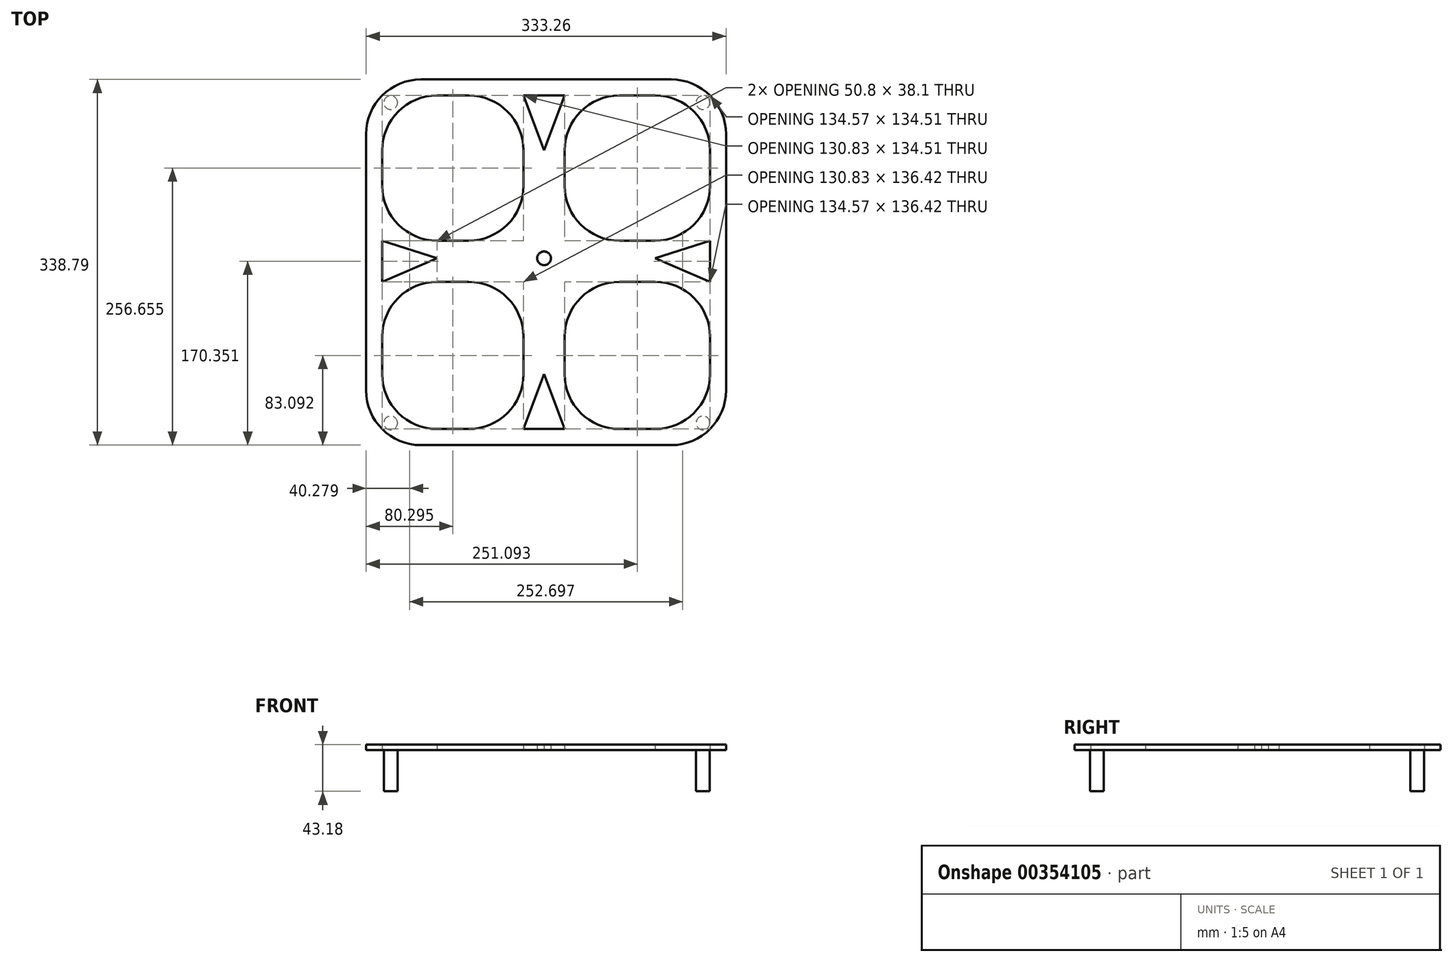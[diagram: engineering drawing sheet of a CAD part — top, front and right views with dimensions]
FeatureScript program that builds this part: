
annotation { "Feature Type Name" : "Feature", "Feature Type Description" : "" }
export const myFeature = defineFeature(function(context is Context, id is Id, definition is map)
    precondition{}
    {
        {
            var Q0;
            Q0=qCreatedBy(makeId("Top.planeOp"),FACE);
            var sketch = newSketch(context, id + "F0", { "sketchPlane" : qUnion([Q0])});
            skLineSegment(sketch, "E0.bottom", {"start": v(102.82, 16.36) * mm, "end": v(69.85, 16.36) * mm});
            skLineSegment(sketch, "E0.top", {"start": v(102.82, -21.74) * mm, "end": v(69.85, -21.74) * mm});
            skPoint(sketch, "E0.middle", {"position": v(0, 0) * mm});
            skLineSegment(sketch, "E1.left", {"start": v(19.05, 100.07) * mm, "end": v(19.05, 67.16) * mm});
            skLineSegment(sketch, "E1.right", {"start": v(-19.05, 100.07) * mm, "end": v(-19.05, 67.16) * mm});
            skPoint(sketch, "E2", {"position": v(-19.05, 16.36) * mm});
            skPoint(sketch, "E3", {"position": v(19.05, 16.36) * mm});
            skPoint(sketch, "E4", {"position": v(19.05, -21.74) * mm});
            skPoint(sketch, "E5", {"position": v(-19.05, -21.74) * mm});
            skLineSegment(sketch, "E6.trimOffspring", {"start": v(-19.05, -72.54) * mm, "end": v(-19.05, -107.36) * mm});
            skLineSegment(sketch, "E7.trimOffspring", {"start": v(-69.85, 16.36) * mm, "end": v(-99.08, 16.36) * mm});
            skLineSegment(sketch, "E8.trimOffspring", {"start": v(19.05, -72.54) * mm, "end": v(19.05, -107.36) * mm});
            skLineSegment(sketch, "E9.trimOffspring", {"start": v(-69.85, -21.74) * mm, "end": v(-99.08, -21.74) * mm});
            skCircle(sketch, "E10", {"center": v(0, 0) * mm, "radius": 6.35 * mm});
            skArc(sketch, "E11.filletArc", {"start": v(-25.4, 16.36) * mm, "mid": v(-20.1, 19.2) * mm, "end": v(-19.55, 25.19) * mm});
            skArc(sketch, "E12.filletArc", {"start": v(-69.85, 16.36) * mm, "mid": v(-33.93, 31.24) * mm, "end": v(-19.05, 67.16) * mm});
            skArc(sketch, "E13.filletArc", {"start": v(19.05, 67.16) * mm, "mid": v(33.93, 31.24) * mm, "end": v(69.85, 16.36) * mm});
            skArc(sketch, "E14.filletArc", {"start": v(69.85, -21.74) * mm, "mid": v(33.93, -36.62) * mm, "end": v(19.05, -72.54) * mm});
            skArc(sketch, "E15.filletArc", {"start": v(-19.05, -72.54) * mm, "mid": v(-33.93, -36.62) * mm, "end": v(-69.85, -21.74) * mm});
            skLineSegment(sketch, "E16", {"start": v(69.85, 150.87) * mm, "end": v(102.82, 150.87) * mm});
            skLineSegment(sketch, "E17", {"start": v(153.62, 100.07) * mm, "end": v(153.62, 67.16) * mm});
            skPoint(sketch, "E18.visualSharp", {"position": v(153.62, 16.36) * mm});
            skArc(sketch, "E18.filletArc", {"start": v(102.82, 16.36) * mm, "mid": v(138.74, 31.24) * mm, "end": v(153.62, 67.16) * mm});
            skPoint(sketch, "E19.visualSharp", {"position": v(19.05, 150.87) * mm});
            skArc(sketch, "E19.filletArc", {"start": v(69.85, 150.87) * mm, "mid": v(33.93, 136) * mm, "end": v(19.05, 100.07) * mm});
            skPoint(sketch, "E20.visualSharp", {"position": v(153.62, 150.87) * mm});
            skArc(sketch, "E20.filletArc", {"start": v(153.62, 100.07) * mm, "mid": v(138.74, 136) * mm, "end": v(102.82, 150.87) * mm});
            skLineSegment(sketch, "E21", {"start": v(-149.88, 67.16) * mm, "end": v(-149.88, 100.07) * mm});
            skLineSegment(sketch, "E22", {"start": v(-99.08, 150.87) * mm, "end": v(-69.85, 150.87) * mm});
            skPoint(sketch, "E23.visualSharp", {"position": v(-149.88, 16.36) * mm});
            skArc(sketch, "E23.filletArc", {"start": v(-149.88, 67.16) * mm, "mid": v(-135, 31.24) * mm, "end": v(-99.08, 16.36) * mm});
            skPoint(sketch, "E24.visualSharp", {"position": v(-149.88, 150.87) * mm});
            skArc(sketch, "E24.filletArc", {"start": v(-99.08, 150.87) * mm, "mid": v(-135, 136) * mm, "end": v(-149.88, 100.07) * mm});
            skPoint(sketch, "E25.visualSharp", {"position": v(-19.05, 150.87) * mm});
            skArc(sketch, "E25.filletArc", {"start": v(-19.05, 100.07) * mm, "mid": v(-33.93, 136) * mm, "end": v(-69.85, 150.87) * mm});
            skLineSegment(sketch, "E26", {"start": v(-149.88, -72.54) * mm, "end": v(-149.88, -107.36) * mm});
            skLineSegment(sketch, "E27", {"start": v(-99.08, -158.16) * mm, "end": v(-69.85, -158.16) * mm});
            skPoint(sketch, "E28.visualSharp", {"position": v(-149.88, -158.16) * mm});
            skArc(sketch, "E28.filletArc", {"start": v(-149.88, -107.36) * mm, "mid": v(-135, -143.28) * mm, "end": v(-99.08, -158.16) * mm});
            skPoint(sketch, "E29.visualSharp", {"position": v(-19.05, -158.16) * mm});
            skPoint(sketch, "E30.visualSharp", {"position": v(-149.88, -21.74) * mm});
            skArc(sketch, "E30.filletArc", {"start": v(-99.08, -21.74) * mm, "mid": v(-135, -36.62) * mm, "end": v(-149.88, -72.54) * mm});
            skArc(sketch, "E31.filletArc", {"start": v(-69.85, -158.16) * mm, "mid": v(-33.93, -143.28) * mm, "end": v(-19.05, -107.36) * mm});
            skLineSegment(sketch, "E32", {"start": v(69.85, -158.16) * mm, "end": v(102.82, -158.16) * mm});
            skLineSegment(sketch, "E33", {"start": v(153.62, -107.36) * mm, "end": v(153.62, -72.54) * mm});
            skPoint(sketch, "E34.visualSharp", {"position": v(19.05, -158.16) * mm});
            skArc(sketch, "E34.filletArc", {"start": v(19.05, -107.36) * mm, "mid": v(33.93, -143.28) * mm, "end": v(69.85, -158.16) * mm});
            skPoint(sketch, "E35.visualSharp", {"position": v(153.62, -158.16) * mm});
            skArc(sketch, "E35.filletArc", {"start": v(102.82, -158.16) * mm, "mid": v(138.74, -143.28) * mm, "end": v(153.62, -107.36) * mm});
            skPoint(sketch, "E36.visualSharp", {"position": v(153.62, -21.74) * mm});
            skArc(sketch, "E36.filletArc", {"start": v(153.62, -72.54) * mm, "mid": v(138.74, -36.62) * mm, "end": v(102.82, -21.74) * mm});
            skLineSegment(sketch, "E37", {"start": v(-113.96, -173.04) * mm, "end": v(117.7, -173.04) * mm});
            skLineSegment(sketch, "E38", {"start": v(168.5, -122.24) * mm, "end": v(168.5, 114.95) * mm});
            skLineSegment(sketch, "E39", {"start": v(117.7, 165.75) * mm, "end": v(-113.96, 165.75) * mm});
            skLineSegment(sketch, "E40", {"start": v(-164.76, 165.75) * mm, "end": v(-164.76, 157.7) * mm});
            skLineSegment(sketch, "E41", {"start": v(-164.76, -122.24) * mm, "end": v(-164.76, 114.95) * mm});
            skPoint(sketch, "E42.visualSharp", {"position": v(-164.76, 165.75) * mm});
            skArc(sketch, "E42.filletArc", {"start": v(-113.96, 165.75) * mm, "mid": v(-149.88, 150.87) * mm, "end": v(-164.76, 114.95) * mm});
            skPoint(sketch, "E43.visualSharp", {"position": v(168.5, 165.75) * mm});
            skArc(sketch, "E43.filletArc", {"start": v(168.5, 114.95) * mm, "mid": v(153.62, 150.87) * mm, "end": v(117.7, 165.75) * mm});
            skPoint(sketch, "E44.visualSharp", {"position": v(168.5, -173.04) * mm});
            skArc(sketch, "E44.filletArc", {"start": v(117.7, -173.04) * mm, "mid": v(153.62, -158.16) * mm, "end": v(168.5, -122.24) * mm});
            skPoint(sketch, "E45.visualSharp", {"position": v(-164.76, -173.04) * mm});
            skArc(sketch, "E45.filletArc", {"start": v(-164.76, -122.24) * mm, "mid": v(-149.88, -158.16) * mm, "end": v(-113.96, -173.04) * mm});
            skLineSegment(sketch, "E46", {"start": v(0, -107.36) * mm, "end": v(-19.05, -158.16) * mm});
            skLineSegment(sketch, "E47", {"start": v(19.05, -158.16) * mm, "end": v(-19.05, -158.16) * mm});
            skLineSegment(sketch, "E48", {"start": v(19.05, -158.16) * mm, "end": v(0, -107.36) * mm});
            skLineSegment(sketch, "E49", {"start": v(0, 100.07) * mm, "end": v(-19.05, 150.87) * mm});
            skLineSegment(sketch, "E50", {"start": v(-19.05, 150.87) * mm, "end": v(19.05, 150.87) * mm});
            skLineSegment(sketch, "E51", {"start": v(19.05, 150.87) * mm, "end": v(0, 100.07) * mm});
            skLineSegment(sketch, "E52", {"start": v(-149.88, 16.36) * mm, "end": v(-149.88, -21.74) * mm});
            skLineSegment(sketch, "E53", {"start": v(102.82, 0) * mm, "end": v(153.62, 16.36) * mm});
            skLineSegment(sketch, "E54", {"start": v(153.62, -21.74) * mm, "end": v(153.62, 16.36) * mm});
            skLineSegment(sketch, "E55", {"start": v(153.62, -21.74) * mm, "end": v(102.82, 0) * mm});
            skLineSegment(sketch, "E56", {"start": v(-99.08, 0) * mm, "end": v(-149.88, -21.74) * mm});
            skLineSegment(sketch, "E57", {"start": v(-149.88, 16.36) * mm, "end": v(-99.08, 0) * mm});
            skSolve(sketch);
        }
        {
            var Q0;
            Q0=makeQuery(id+"F0.imprint","IMPRINT",FACE,{"disambiguationData":[TD([[makeQuery(id+"F0.imprint","IMPRINT",EDGE,{"derivedFrom":sQuery(id+"F0.wireOp",EDGE,"E0.bottom")}),1.0]])]});
            var Q1;
            Q1=makeQuery(id+"F0.imprint","IMPRINT",FACE,{"disambiguationData":[TD([[makeQuery(id+"F0.imprint","IMPRINT",EDGE,{"derivedFrom":sQuery(id+"F0.wireOp",EDGE,"HhHGXukK-88LZ-Qlhe-yOUI-ivqigiWirlnT")}),-1.0]])]});
            var Q2;
            Q2=makeQuery(id+"F0.imprint","IMPRINT",FACE,{"disambiguationData":[TD([[makeQuery(id+"F0.imprint","IMPRINT",EDGE,{"derivedFrom":sQuery(id+"F0.wireOp",EDGE,"GWZDvsel-j2r0-KArF-ZehE-5JIaTQembRwq")}),-1.0]])]});
            var Q3;
            Q3=makeQuery(id+"F0.imprint","IMPRINT",FACE,{"disambiguationData":[TD([[makeQuery(id+"F0.imprint","IMPRINT",EDGE,{"derivedFrom":sQuery(id+"F0.wireOp",EDGE,"nUYmWv30-9dqW-i0KR-sggg-cQleaPBZfBGV")}),-1.0]])]});
            var Q4;
            Q4=makeQuery(id+"F0.imprint","IMPRINT",FACE,{"disambiguationData":[TD([[makeQuery(id+"F0.imprint","IMPRINT",EDGE,{"derivedFrom":sQuery(id+"F0.wireOp",EDGE,"eROQzvXG-G305-7KOf-UkAC-neXF0GO081Xd")}),-1.0]])]});
            extrude(context, id + "F1", {"entities" : qUnion([Q0, Q1, Q2, Q3, Q4]), "depth" : 5.08 * mm});
        }
        {
            var Q0;
            Q0=qCreatedBy(makeId("Top.planeOp"),FACE);
            var sketch = newSketch(context, id + "F2", { "sketchPlane" : qUnion([Q0])});
            skCircle(sketch, "E58", {"center": v(-142.03, -152.5) * mm, "radius": 6.35 * mm});
            skCircle(sketch, "E59", {"center": v(-142.03, 144.24) * mm, "radius": 6.35 * mm});
            skCircle(sketch, "E60", {"center": v(147.1, 144.24) * mm, "radius": 6.35 * mm});
            skCircle(sketch, "E61", {"center": v(147.1, -152.5) * mm, "radius": 6.35 * mm});
            skSolve(sketch);
        }
        {
            var Q0;
            Q0 = qSketchRegion(id + "F2", true);
            extrude(context, id + "F3", {"entities" : qUnion([Q0]), "operationType" : NewBodyOperationType.ADD, "oppositeDirection" : true, "depth" : 38.1 * mm});
        }
    });
